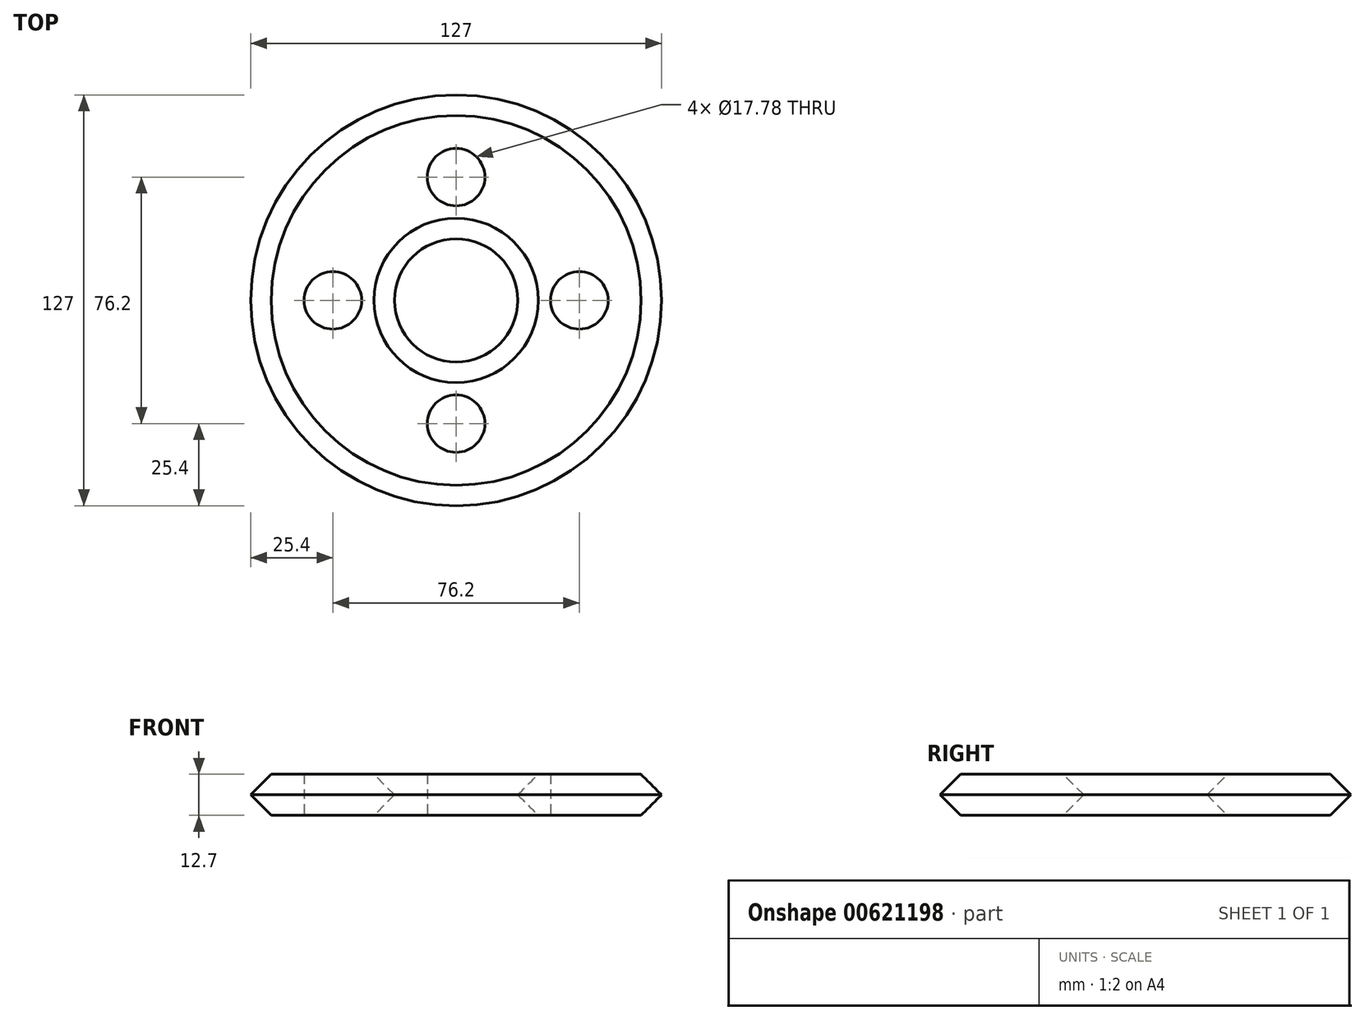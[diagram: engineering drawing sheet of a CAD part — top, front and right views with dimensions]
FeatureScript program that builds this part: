
annotation { "Feature Type Name" : "Feature", "Feature Type Description" : "" }
export const myFeature = defineFeature(function(context is Context, id is Id, definition is map)
    precondition{}
    {
        {
            var Q0;
            Q0=qCreatedBy(makeId("Top.planeOp"),FACE);
            var sketch = newSketch(context, id + "F0", { "sketchPlane" : qUnion([Q0])});
            skCircle(sketch, "E0", {"center": v(0, 0) * mm, "radius": 63.5 * mm});
            skCircle(sketch, "E1", {"center": v(0, 0) * mm, "radius": 19.05 * mm});
            skSolve(sketch);
        }
        {
            var Q0;
            Q0=makeQuery(id+"F0.imprint","IMPRINT",FACE,{"disambiguationData":[TD([[makeQuery(id+"F0.imprint","IMPRINT",EDGE,{"derivedFrom":sQuery(id+"F0.wireOp",EDGE,"E0")}),1.0]])]});
            extrude(context, id + "F1", {"entities" : qUnion([Q0]), "depth" : 12.7 * mm, "offsetDistance" : 25.4 * mm});
        }
        {
            var Q0;
            Q0=qCreatedBy(makeId("Top.planeOp"),FACE);
            var sketch = newSketch(context, id + "F2", { "sketchPlane" : qUnion([Q0])});
            skPoint(sketch, "E2", {"position": v(0, 38.1) * mm});
            skPoint(sketch, "E3", {"position": v(38.1, 0) * mm});
            skPoint(sketch, "E4", {"position": v(0, -38.1) * mm});
            skPoint(sketch, "E5", {"position": v(-38.1, 0) * mm});
            skSolve(sketch);
        }
        {
            var Q0;
            Q0=sQuery(id+"F2.wireOp",VERTEX,"E2");
            var Q1;
            Q1=sQuery(id+"F2.wireOp",VERTEX,"E5");
            var Q2;
            Q2=sQuery(id+"F2.wireOp",VERTEX,"E4");
            var Q3;
            Q3=sQuery(id+"F2.wireOp",VERTEX,"E3");
            var Q4;
            Q4=makeQuery(id+"F1.opExtrude","SWEPT_BODY",BODY,{"disambiguationData":[OSD([sQuery(id+"F0.wireOp",EDGE,"E0"),sQuery(id+"F0.wireOp",EDGE,"E1")])]});
            hole(context, id + "F3", {"style" : HoleStyle.SIMPLE, "endStyle" : HoleEndStyle.THROUGH, "oppositeDirection" : true, "holeDiameter" : 17.78 * mm, "majorDiameter" : 6.35 * mm, "isTappedThrough" : true, "tappedDepth" : 12.7 * mm, "tapClearance" : 3, "locations" : qUnion([Q0, Q1, Q2, Q3]), "scope" : qUnion([Q4])});
        }
        {
            var Q0;
            Q0=makeQuery(id+"F3.hole-1.boolean.opBoolean","INTERSECT",EDGE,{"derivedFrom":[makeQuery(id+"F1.opExtrude","CAP_FACE",FACE,{"disambiguationData":[OSD([sQuery(id+"F0.wireOp",EDGE,"E0"),sQuery(id+"F0.wireOp",EDGE,"E1")])],"isStart":false}),makeQuery(id+"F3.hole-1.opRevolve","SWEPT_FACE",FACE,{"disambiguationData":[OSD([sQuery(id+"F3.hole-1.sketch.wireOp",EDGE,"core_line_2")])]})]});
            var Q1;
            Q1=makeQuery(id+"F3.hole-1.boolean.opBoolean","COPY",EDGE,{"derivedFrom":makeQuery(id+"F3.hole-1.opRevolve","SWEPT_EDGE",EDGE,{"disambiguationData":[OSD([sQuery(id+"F3.hole-1.sketch.wireOp",EDGE,"core_line_2"),sQuery(id+"F3.hole-1.sketch.wireOp",EDGE,"core_line_3")])]})});
            var Q2;
            Q2=makeQuery(id+"F1.opExtrude","CAP_EDGE",EDGE,{"disambiguationData":[OSD([sQuery(id+"F0.wireOp",EDGE,"E1")])],"isStart":true});
            var Q3;
            Q3=makeQuery(id+"F1.opExtrude","CAP_EDGE",EDGE,{"disambiguationData":[OSD([sQuery(id+"F0.wireOp",EDGE,"E1")])],"isStart":false});
            var Q4;
            Q4=makeQuery(id+"F3.hole-0.boolean.opBoolean","INTERSECT",EDGE,{"derivedFrom":[makeQuery(id+"F1.opExtrude","CAP_FACE",FACE,{"disambiguationData":[OSD([sQuery(id+"F0.wireOp",EDGE,"E0"),sQuery(id+"F0.wireOp",EDGE,"E1")])],"isStart":false}),makeQuery(id+"F3.hole-0.opRevolve","SWEPT_FACE",FACE,{"disambiguationData":[OSD([sQuery(id+"F3.hole-0.sketch.wireOp",EDGE,"core_line_2")])]})]});
            var Q5;
            Q5=makeQuery(id+"F3.hole-0.boolean.opBoolean","COPY",EDGE,{"derivedFrom":makeQuery(id+"F3.hole-0.opRevolve","SWEPT_EDGE",EDGE,{"disambiguationData":[OSD([sQuery(id+"F3.hole-0.sketch.wireOp",EDGE,"core_line_2"),sQuery(id+"F3.hole-0.sketch.wireOp",EDGE,"core_line_3")])]})});
            var Q6;
            Q6=makeQuery(id+"F3.hole-3.boolean.opBoolean","COPY",EDGE,{"derivedFrom":makeQuery(id+"F3.hole-3.opRevolve","SWEPT_EDGE",EDGE,{"disambiguationData":[OSD([sQuery(id+"F3.hole-3.sketch.wireOp",EDGE,"core_line_2"),sQuery(id+"F3.hole-3.sketch.wireOp",EDGE,"core_line_3")])]})});
            var Q7;
            Q7=makeQuery(id+"F3.hole-3.boolean.opBoolean","INTERSECT",EDGE,{"derivedFrom":[makeQuery(id+"F1.opExtrude","CAP_FACE",FACE,{"disambiguationData":[OSD([sQuery(id+"F0.wireOp",EDGE,"E0"),sQuery(id+"F0.wireOp",EDGE,"E1")])],"isStart":false}),makeQuery(id+"F3.hole-3.opRevolve","SWEPT_FACE",FACE,{"disambiguationData":[OSD([sQuery(id+"F3.hole-3.sketch.wireOp",EDGE,"core_line_2")])]})]});
            var Q8;
            Q8=makeQuery(id+"F3.hole-2.boolean.opBoolean","INTERSECT",EDGE,{"derivedFrom":[makeQuery(id+"F1.opExtrude","CAP_FACE",FACE,{"disambiguationData":[OSD([sQuery(id+"F0.wireOp",EDGE,"E0"),sQuery(id+"F0.wireOp",EDGE,"E1")])],"isStart":false}),makeQuery(id+"F3.hole-2.opRevolve","SWEPT_FACE",FACE,{"disambiguationData":[OSD([sQuery(id+"F3.hole-2.sketch.wireOp",EDGE,"core_line_2")])]})]});
            var Q9;
            Q9=makeQuery(id+"F3.hole-2.boolean.opBoolean","COPY",EDGE,{"derivedFrom":makeQuery(id+"F3.hole-2.opRevolve","SWEPT_EDGE",EDGE,{"disambiguationData":[OSD([sQuery(id+"F3.hole-2.sketch.wireOp",EDGE,"core_line_2"),sQuery(id+"F3.hole-2.sketch.wireOp",EDGE,"core_line_3")])]})});
            var Q10;
            Q10=makeQuery(id+"F1.opExtrude","CAP_EDGE",EDGE,{"disambiguationData":[OSD([sQuery(id+"F0.wireOp",EDGE,"E0")])],"isStart":false});
            var Q11;
            Q11=makeQuery(id+"F1.opExtrude","CAP_EDGE",EDGE,{"disambiguationData":[OSD([sQuery(id+"F0.wireOp",EDGE,"E0")])],"isStart":true});
            chamfer(context, id + "F4", {"entities" : qUnion([Q0, Q1, Q2, Q3, Q4, Q5, Q6, Q7, Q8, Q9, Q10, Q11]), "width" : 6.35 * mm, "tangentPropagation" : true});
        }
    });
